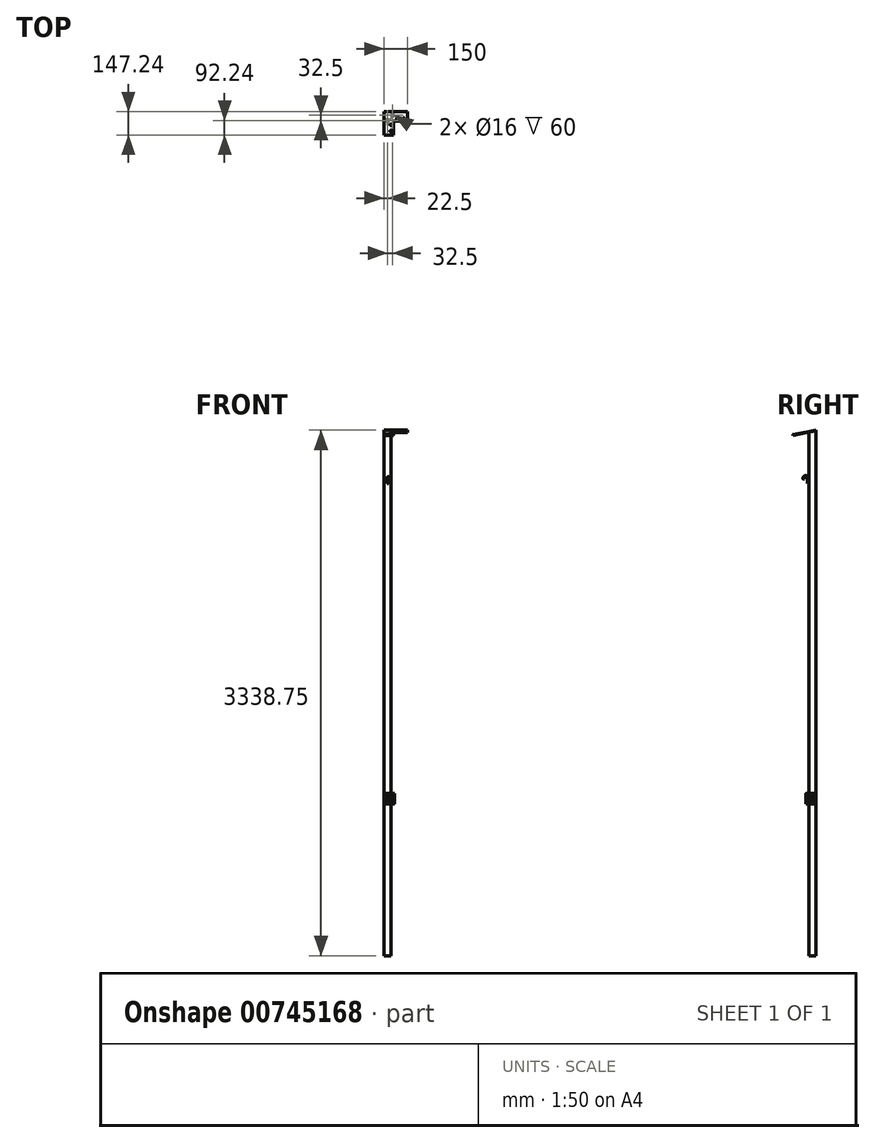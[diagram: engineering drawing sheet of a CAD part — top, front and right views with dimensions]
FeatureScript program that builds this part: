
annotation { "Feature Type Name" : "Feature", "Feature Type Description" : "" }
export const myFeature = defineFeature(function(context is Context, id is Id, definition is map)
    precondition{}
    {
        {
            var Q0;
            Q0=qCreatedBy(makeId("Top.planeOp"),FACE);
            var sketch = newSketch(context, id + "F0", { "sketchPlane" : qUnion([Q0])});
            skLineSegment(sketch, "E0.bottom", {"start": v(22.5, -22.5) * mm, "end": v(-22.5, -22.5) * mm});
            skLineSegment(sketch, "E0.top", {"start": v(22.5, 22.5) * mm, "end": v(-22.5, 22.5) * mm});
            skLineSegment(sketch, "E0.left", {"start": v(22.5, -22.5) * mm, "end": v(22.5, 22.5) * mm});
            skLineSegment(sketch, "E0.right", {"start": v(-22.5, -22.5) * mm, "end": v(-22.5, 22.5) * mm});
            skPoint(sketch, "E0.middle", {"position": v(0, 0) * mm});
            skSolve(sketch);
        }
        {
            var Q0;
            Q0 = qSketchRegion(id + "F0", true);
            extrude(context, id + "F1", {"entities" : qUnion([Q0]), "depth" : 3330 * mm, "offsetDistance" : 25 * mm});
        }
        {
            var Q0;
            Q0=qCreatedBy(makeId("Top.planeOp"),FACE);
            cPlane(context, id + "F2", {"entities" : qUnion([Q0]), "cplaneType" : CPlaneType.OFFSET, "offset" : 965 * mm, "width" : 150 * mm, "height" : 150 * mm});
        }
        {
            var Q0;
            Q0=qCreatedBy(id+"F2.planeOp",FACE);
            var sketch = newSketch(context, id + "F3", { "sketchPlane" : qUnion([Q0])});
            skLineSegment(sketch, "E1", {"start": v(0, -22.5) * mm, "end": v(0, -32.5) * mm});
            skCircle(sketch, "E2", {"center": v(0, -32.5) * mm, "radius": 10 * mm});
            skLineSegment(sketch, "E3", {"start": v(0, 0) * mm, "end": v(22.5, 0) * mm});
            skLineSegment(sketch, "E4", {"start": v(22.5, 0) * mm, "end": v(32.5, 0) * mm});
            skCircle(sketch, "E5", {"center": v(32.5, 0) * mm, "radius": 10 * mm});
            skLineSegment(sketch, "E6", {"start": v(32.5, 0) * mm, "end": v(32.5, 2) * mm});
            skLineSegment(sketch, "E7", {"start": v(32.5, 0) * mm, "end": v(32.5, -2) * mm});
            skLineSegment(sketch, "E8", {"start": v(0, -32.5) * mm, "end": v(2, -32.5) * mm});
            skLineSegment(sketch, "E9", {"start": v(0, -32.5) * mm, "end": v(-2, -32.5) * mm});
            skLineSegment(sketch, "E10", {"start": v(32.5, -2) * mm, "end": v(22.5, -2) * mm});
            skLineSegment(sketch, "E11", {"start": v(32.5, 2) * mm, "end": v(22.5, 2) * mm});
            skLineSegment(sketch, "E12", {"start": v(2, -32.5) * mm, "end": v(2, -22.5) * mm});
            skLineSegment(sketch, "E13", {"start": v(-2, -32.5) * mm, "end": v(-2, -22.5) * mm});
            skLineSegment(sketch, "E14", {"start": v(32.5, -2) * mm, "end": v(32.5, -10) * mm});
            skLineSegment(sketch, "E15", {"start": v(32.5, -10) * mm, "end": v(22.5, -10) * mm});
            skLineSegment(sketch, "E16", {"start": v(32.5, 2) * mm, "end": v(32.5, 10) * mm});
            skLineSegment(sketch, "E17", {"start": v(32.5, 10) * mm, "end": v(22.5, 10) * mm});
            skLineSegment(sketch, "E18", {"start": v(22.5, 10) * mm, "end": v(22.5, -10) * mm});
            skLineSegment(sketch, "E19", {"start": v(2, -32.5) * mm, "end": v(10, -32.5) * mm});
            skLineSegment(sketch, "E20", {"start": v(10, -32.5) * mm, "end": v(10, -22.5) * mm});
            skLineSegment(sketch, "E21", {"start": v(10, -22.5) * mm, "end": v(-10, -22.5) * mm});
            skLineSegment(sketch, "E22", {"start": v(-10, -22.5) * mm, "end": v(-10, -32.5) * mm});
            skSolve(sketch);
        }
        {
            var Q0;
            Q0 = qSketchRegion(id + "F3", true);
            extrude(context, id + "F4", {"entities" : qUnion([Q0]), "operationType" : NewBodyOperationType.ADD, "depth" : 5 * mm, "offsetDistance" : 25 * mm});
        }
        {
            var Q0;
            Q0=makeQuery(id+"F4.opExtrude","CAP_FACE",FACE,{"disambiguationData":[OSD([sQuery(id+"F3.wireOp",EDGE,"E5")])],"isStart":false});
            var sketch = newSketch(context, id + "F5", { "sketchPlane" : qUnion([Q0])});
            skCircle(sketch, "E23", {"center": v(32.5, 0) * mm, "radius": 10 * mm});
            skCircle(sketch, "E24", {"center": v(0, -32.5) * mm, "radius": 10 * mm});
            skCircle(sketch, "E25", {"center": v(32.5, 0) * mm, "radius": 8 * mm});
            skCircle(sketch, "E26", {"center": v(0, -32.5) * mm, "radius": 8 * mm});
            skLineSegment(sketch, "E27", {"start": v(32.5, 10) * mm, "end": v(22.5, 10) * mm});
            skLineSegment(sketch, "E28", {"start": v(22.5, 10) * mm, "end": v(22.5, -10) * mm});
            skLineSegment(sketch, "E29", {"start": v(22.5, -10) * mm, "end": v(32.5, -10) * mm});
            skLineSegment(sketch, "E30", {"start": v(0, -32.5) * mm, "end": v(10, -32.5) * mm});
            skLineSegment(sketch, "E31", {"start": v(10, -32.5) * mm, "end": v(10, -22.5) * mm});
            skLineSegment(sketch, "E32", {"start": v(10, -22.5) * mm, "end": v(-10, -22.5) * mm});
            skLineSegment(sketch, "E33", {"start": v(-10, -22.5) * mm, "end": v(-10, -32.5) * mm});
            skSolve(sketch);
        }
        {
            var Q0;
            Q0 = qSketchRegion(id + "F5", true);
            extrude(context, id + "F6", {"entities" : qUnion([Q0]), "operationType" : NewBodyOperationType.ADD, "depth" : 60 * mm, "offsetDistance" : 25 * mm});
        }
        {
            var Q0;
            Q0=makeQuery(id+"F1.opExtrude","CAP_EDGE",EDGE,{"disambiguationData":[OSD([sQuery(id+"F0.wireOp",EDGE,"E0.bottom")])],"isStart":false});
            cPlane(context, id + "F7", {"entities" : qUnion([Q0]), "cplaneType" : CPlaneType.LINE_ANGLE, "offset" : 25 * mm, "angle" : 101 * degree, "oppositeDirection" : true, "width" : 150 * mm, "height" : 150 * mm});
        }
        {
            var Q0;
            Q0=makeQuery(id+"F1.opExtrude","CAP_FACE",FACE,{"disambiguationData":[OSD([sQuery(id+"F0.wireOp",EDGE,"E0.bottom"),sQuery(id+"F0.wireOp",EDGE,"E0.top"),sQuery(id+"F0.wireOp",EDGE,"E0.left"),sQuery(id+"F0.wireOp",EDGE,"E0.right")])],"isStart":false});
            var sketch = newSketch(context, id + "F8", { "sketchPlane" : qUnion([Q0])});
            skLineSegment(sketch, "E34.bottom", {"start": v(-22.5, 22.5) * mm, "end": v(22.5, 22.5) * mm});
            skLineSegment(sketch, "E34.top", {"start": v(-22.5, -22.5) * mm, "end": v(22.5, -22.5) * mm});
            skLineSegment(sketch, "E34.left", {"start": v(-22.5, 22.5) * mm, "end": v(-22.5, -22.5) * mm});
            skLineSegment(sketch, "E34.right", {"start": v(22.5, 22.5) * mm, "end": v(22.5, -22.5) * mm});
            skSolve(sketch);
        }
        {
            var Q0;
            Q0=qCreatedBy(id+"F7.planeOp",FACE);
            var sketch = newSketch(context, id + "F9", { "sketchPlane" : qUnion([Q0])});
            skLineSegment(sketch, "E35.bottom", {"start": v(-22.5, -659.15) * mm, "end": v(22.5, -659.15) * mm});
            skLineSegment(sketch, "E35.top", {"start": v(-22.5, -613.3) * mm, "end": v(22.5, -613.3) * mm});
            skLineSegment(sketch, "E35.left", {"start": v(-22.5, -659.15) * mm, "end": v(-22.5, -613.3) * mm});
            skLineSegment(sketch, "E35.right", {"start": v(22.5, -659.15) * mm, "end": v(22.5, -613.3) * mm});
            skSolve(sketch);
        }
        {
            var Q0;
            Q0=makeQuery(id+"F9.imprint","IMPRINT",FACE,{"disambiguationData":[TD([[makeQuery(id+"F9.imprint","IMPRINT",EDGE,{"derivedFrom":sQuery(id+"F9.wireOp",EDGE,"E35.bottom")}),1.0]])]});
            extrude(context, id + "F10", {"entities" : qUnion([Q0]), "operationType" : NewBodyOperationType.ADD, "depth" : 25 * mm, "offsetDistance" : 25 * mm});
        }
        {
            var Q0;
            Q0=qCreatedBy(id+"F7.planeOp",FACE);
            var sketch = newSketch(context, id + "F11", { "sketchPlane" : qUnion([Q0])});
            skLineSegment(sketch, "E36.bottom", {"start": v(-22.5, -659.15) * mm, "end": v(37.5, -659.15) * mm});
            skLineSegment(sketch, "E36.top", {"start": v(-22.5, -599.15) * mm, "end": v(37.5, -599.15) * mm});
            skLineSegment(sketch, "E36.left", {"start": v(-22.5, -659.15) * mm, "end": v(-22.5, -599.15) * mm});
            skLineSegment(sketch, "E36.right", {"start": v(37.5, -659.15) * mm, "end": v(37.5, -599.15) * mm});
            skLineSegment(sketch, "E37.bottom", {"start": v(37.5, -659.15) * mm, "end": v(127.5, -659.15) * mm});
            skLineSegment(sketch, "E37.top", {"start": v(37.5, -599.15) * mm, "end": v(127.5, -599.15) * mm});
            skLineSegment(sketch, "E37.right", {"start": v(127.5, -659.15) * mm, "end": v(127.5, -599.15) * mm});
            skLineSegment(sketch, "E38.top", {"start": v(-22.5, -509.15) * mm, "end": v(37.5, -509.15) * mm});
            skLineSegment(sketch, "E38.left", {"start": v(-22.5, -599.15) * mm, "end": v(-22.5, -509.15) * mm});
            skLineSegment(sketch, "E38.right", {"start": v(37.5, -599.15) * mm, "end": v(37.5, -509.15) * mm});
            skLineSegment(sketch, "E39", {"start": v(-22.5, -659.15) * mm, "end": v(-22.5, -509.15) * mm});
            skSolve(sketch);
        }
        {
            var Q0;
            Q0 = qSketchRegion(id + "F11", true);
            extrude(context, id + "F12", {"entities" : qUnion([Q0]), "operationType" : NewBodyOperationType.ADD, "depth" : 5 * mm, "offsetDistance" : 25 * mm});
        }
        {
            var Q0;
            Q0=makeQuery(id+"F12.boolean.opBoolean","MERGE",FACE,{"derivedFrom":[makeQuery(id+"F10.opExtrude","CAP_FACE",FACE,{"disambiguationData":[OSD([sQuery(id+"F9.wireOp",EDGE,"E35.bottom"),sQuery(id+"F9.wireOp",EDGE,"E35.top"),sQuery(id+"F9.wireOp",EDGE,"E35.left"),sQuery(id+"F9.wireOp",EDGE,"E35.right")])],"isStart":true}),makeQuery(id+"F12.opExtrude","CAP_FACE",FACE,{"disambiguationData":[OSD([sQuery(id+"F11.wireOp",EDGE,"E36.bottom"),sQuery(id+"F11.wireOp",EDGE,"E37.bottom"),sQuery(id+"F11.wireOp",EDGE,"E37.top"),sQuery(id+"F11.wireOp",EDGE,"E37.right"),sQuery(id+"F11.wireOp",EDGE,"E38.top"),sQuery(id+"F11.wireOp",EDGE,"E38.right"),sQuery(id+"F11.wireOp",EDGE,"E39")])],"isStart":true})]});
            var sketch = newSketch(context, id + "F13", { "sketchPlane" : qUnion([Q0])});
            skLineSegment(sketch, "E40", {"start": v(37.5, 509.15) * mm, "end": v(37.5, 534.15) * mm});
            skLineSegment(sketch, "E41", {"start": v(37.5, 534.15) * mm, "end": v(22.5, 534.15) * mm});
            skLineSegment(sketch, "E42", {"start": v(22.5, 534.15) * mm, "end": v(22.5, 574.15) * mm});
            skCircle(sketch, "E43", {"center": v(22.5, 534.15) * mm, "radius": 6 * mm});
            skCircle(sketch, "E44", {"center": v(22.5, 574.15) * mm, "radius": 6 * mm});
            skLineSegment(sketch, "E45", {"start": v(127.5, 599.15) * mm, "end": v(102.5, 599.15) * mm});
            skLineSegment(sketch, "E46", {"start": v(102.5, 599.15) * mm, "end": v(102.5, 614.15) * mm});
            skLineSegment(sketch, "E47", {"start": v(102.5, 614.15) * mm, "end": v(62.5, 614.15) * mm});
            skCircle(sketch, "E48", {"center": v(102.5, 614.15) * mm, "radius": 6 * mm});
            skCircle(sketch, "E49", {"center": v(62.5, 614.15) * mm, "radius": 6 * mm});
            skSolve(sketch);
        }
        {
            var Q0;
            Q0 = qSketchRegion(id + "F13", true);
            extrude(context, id + "F14", {"entities" : qUnion([Q0]), "operationType" : NewBodyOperationType.REMOVE, "oppositeDirection" : true, "depth" : 25 * mm, "offsetDistance" : 25 * mm});
        }
        {
            var Q0;
            Q0=qCreatedBy(makeId("Top.planeOp"),FACE);
            cPlane(context, id + "F15", {"entities" : qUnion([Q0]), "cplaneType" : CPlaneType.OFFSET, "offset" : 3000 * mm, "width" : 150 * mm, "height" : 150 * mm});
        }
        {
            var Q0;
            Q0=qCreatedBy(id+"F15.planeOp",FACE);
            var sketch = newSketch(context, id + "F16", { "sketchPlane" : qUnion([Q0])});
            skCircle(sketch, "E50", {"center": v(0, -27.5) * mm, "radius": 5 * mm});
            skLineSegment(sketch, "E51", {"start": v(-22.5, -22.5) * mm, "end": v(22.5, -22.5) * mm});
            skLineSegment(sketch, "E52", {"start": v(0, -31.5) * mm, "end": v(0, -22.5) * mm});
            skLineSegment(sketch, "E53", {"start": v(-5, -27.68) * mm, "end": v(-5, -22.5) * mm});
            skLineSegment(sketch, "E54", {"start": v(-5, -22.5) * mm, "end": v(5, -22.5) * mm});
            skLineSegment(sketch, "E55", {"start": v(5, -22.5) * mm, "end": v(5, -27.5) * mm});
            skLineSegment(sketch, "E56", {"start": v(5, -22.5) * mm, "end": v(-5, -22.5) * mm});
            skSolve(sketch);
        }
        {
            var Q0;
            Q0=qCreatedBy(makeId("Top.planeOp"),FACE);
            var sketch = newSketch(context, id + "F17", { "sketchPlane" : qUnion([Q0])});
            skLineSegment(sketch, "E57.bottom", {"start": v(-22.5, 22.5) * mm, "end": v(127.5, 22.5) * mm});
            skLineSegment(sketch, "E57.top", {"start": v(-22.5, 27.27) * mm, "end": v(127.5, 27.27) * mm});
            skLineSegment(sketch, "E57.left", {"start": v(-22.5, 22.5) * mm, "end": v(-22.5, 27.27) * mm});
            skLineSegment(sketch, "E57.right", {"start": v(127.5, 22.5) * mm, "end": v(127.5, 27.27) * mm});
            skSolve(sketch);
        }
        {
            var Q0;
            Q0 = qSketchRegion(id + "F17", true);
            extrude(context, id + "F18", {"entities" : qUnion([Q0]), "operationType" : NewBodyOperationType.REMOVE, "depth" : 3358.7 * mm, "offsetDistance" : 25 * mm});
        }
        {
            var Q0;
            Q0 = qSketchRegion(id + "F16", true);
            extrude(context, id + "F19", {"entities" : qUnion([Q0]), "operationType" : NewBodyOperationType.ADD, "depth" : 30 * mm, "offsetDistance" : 25 * mm});
        }
        {
            var Q0;
            Q0=makeQuery(id+"F19.opExtrude","CAP_FACE",FACE,{"disambiguationData":[OSD([sQuery(id+"F16.wireOp",EDGE,"E50"),sQuery(id+"F16.wireOp",EDGE,"E53"),sQuery(id+"F16.wireOp",EDGE,"E55"),sQuery(id+"F16.wireOp",EDGE,"E56")])],"isStart":false});
            var sketch = newSketch(context, id + "F20", { "sketchPlane" : qUnion([Q0])});
            skArc(sketch, "E58.0", {"start": v(-5, -27.5) * mm, "mid": v(0, -32.5) * mm, "end": v(5, -27.5) * mm});
            skArc(sketch, "E59.MirrorCS", {"start": v(-5, -27.5) * mm, "mid": v(0, -22.5) * mm, "end": v(5, -27.5) * mm});
            skSolve(sketch);
        }
        {
            var Q0;
            Q0=qCreatedBy(makeId("Right.planeOp"),FACE);
            var sketch = newSketch(context, id + "F21", { "sketchPlane" : qUnion([Q0])});
            skLineSegment(sketch, "E60", {"start": v(-27.5, 3030) * mm, "end": v(-57.5, 3030) * mm});
            skArc(sketch, "E61", {"start": v(-27.5, 3030) * mm, "mid": v(-42.5, 3045) * mm, "end": v(-57.5, 3030) * mm});
            skSolve(sketch);
        }
        {
            var Q0;
            {var subQ0=sQuery(id+"F20.wireOp",EDGE,"E58.0");Q0=makeQuery(id+"F20.imprint","IMPRINT",FACE,{"disambiguationData":[TD([[makeQuery(id+"F20.imprint","IMPRINT",EDGE,{"derivedFrom":subQ0}),1.0]])]});}
            var Q1;
            Q1=sQuery(id+"F21.wireOp",EDGE,"E61");
            sweep(context, id + "F22", {"operationType" : NewBodyOperationType.ADD, "profiles" : qUnion([Q0]), "path" : qUnion([Q1])});
        }
    });
